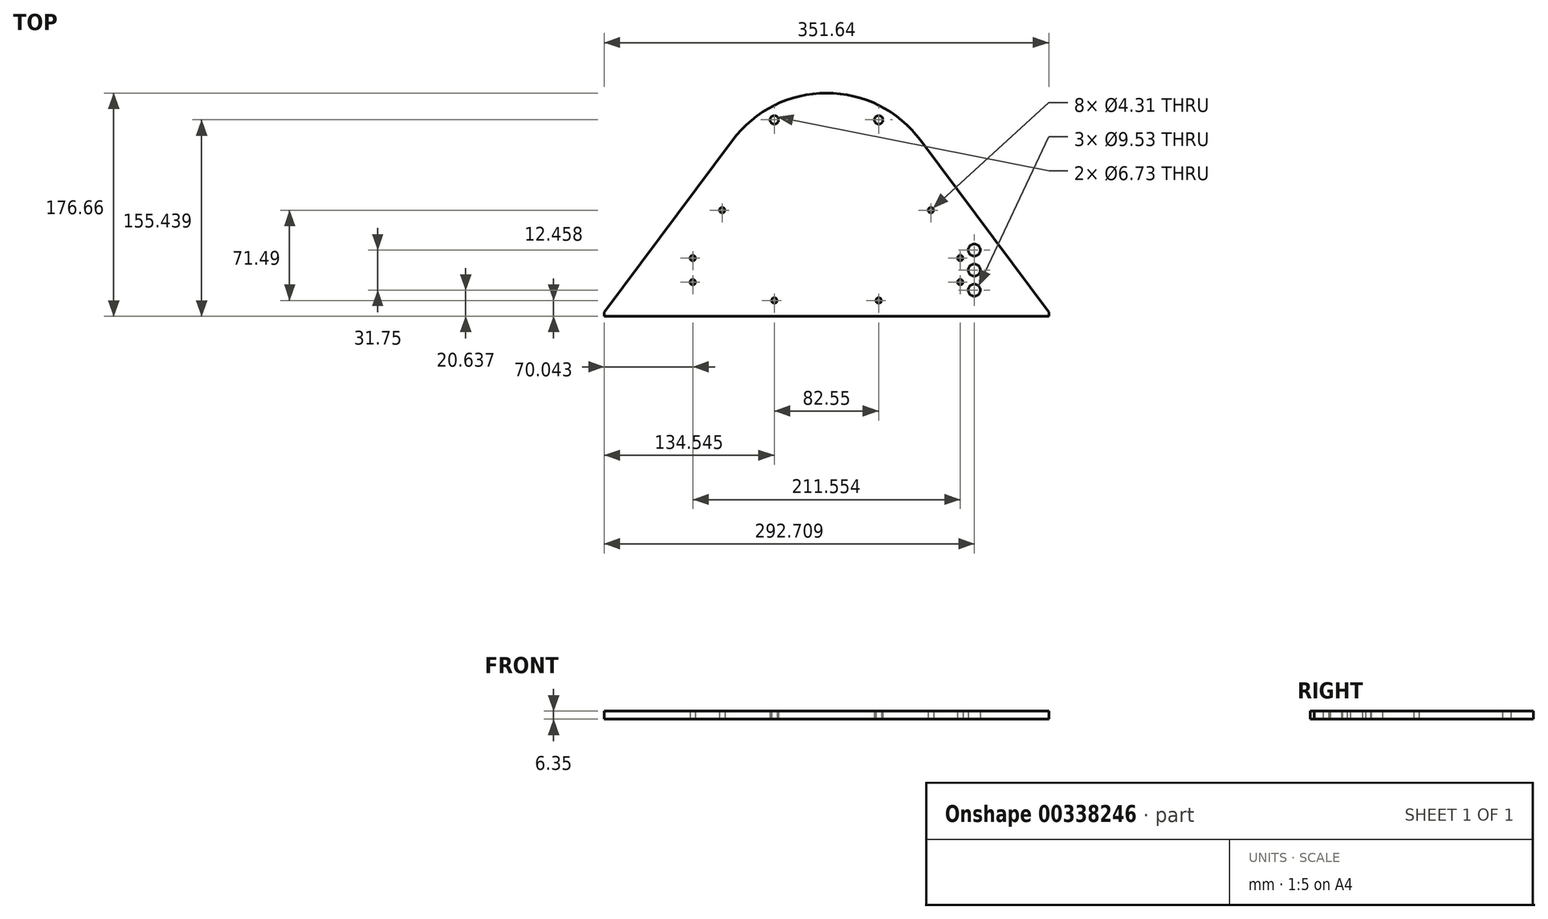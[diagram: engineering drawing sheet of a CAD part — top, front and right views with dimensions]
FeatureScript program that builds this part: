
annotation { "Feature Type Name" : "Feature", "Feature Type Description" : "" }
export const myFeature = defineFeature(function(context is Context, id is Id, definition is map)
    precondition{}
    {
        {
            var Q0;
            Q0=qCreatedBy(makeId("Top.planeOp"),FACE);
            var sketch = newSketch(context, id + "F0", { "sketchPlane" : qUnion([Q0])});
            skLineSegment(sketch, "E0", {"start": v(0, 0) * mm, "end": v(351.64, 0) * mm});
            skLineSegment(sketch, "E1", {"start": v(351.64, 0) * mm, "end": v(351.64, 3.18) * mm});
            skLineSegment(sketch, "E2", {"start": v(351.64, 3.17) * mm, "end": v(250.16, 139.35) * mm});
            skLineSegment(sketch, "E3", {"start": v(175.82, 0) * mm, "end": v(175.82, 83.95) * mm, "construction": true});
            skArc(sketch, "E4", {"start": v(250.16, 139.35) * mm, "mid": v(175.82, 176.66) * mm, "end": v(101.48, 139.35) * mm});
            skLineSegment(sketch, "E5", {"start": v(175.82, 83.95) * mm, "end": v(258.37, 83.95) * mm, "construction": true});
            skLineSegment(sketch, "E6", {"start": v(175.82, 83.95) * mm, "end": v(134.55, 155.44) * mm, "construction": true});
            skLineSegment(sketch, "E7", {"start": v(175.82, 83.95) * mm, "end": v(217.1, 155.44) * mm, "construction": true});
            skLineSegment(sketch, "E8", {"start": v(175.82, 83.95) * mm, "end": v(175.82, 155.44) * mm, "construction": true});
            skLineSegment(sketch, "E9", {"start": v(134.55, 155.44) * mm, "end": v(217.1, 155.44) * mm, "construction": true});
            skCircle(sketch, "E10", {"center": v(134.55, 155.44) * mm, "radius": 10.16 * mm, "construction": true});
            skLineSegment(sketch, "E11", {"start": v(0, 0) * mm, "end": v(0, 3.17) * mm});
            skLineSegment(sketch, "E12", {"start": v(0, 3.17) * mm, "end": v(101.48, 139.35) * mm});
            skLineSegment(sketch, "E13", {"start": v(175.82, 83.95) * mm, "end": v(217.1, 12.46) * mm, "construction": true});
            skLineSegment(sketch, "E14", {"start": v(217.1, 12.46) * mm, "end": v(258.37, 83.95) * mm, "construction": true});
            skLineSegment(sketch, "E15", {"start": v(258.37, 83.95) * mm, "end": v(217.1, 155.44) * mm, "construction": true});
            skLineSegment(sketch, "E16", {"start": v(134.55, 155.44) * mm, "end": v(93.27, 83.95) * mm, "construction": true});
            skLineSegment(sketch, "E17", {"start": v(93.27, 83.95) * mm, "end": v(175.82, 83.95) * mm, "construction": true});
            skLineSegment(sketch, "E18", {"start": v(175.82, 83.95) * mm, "end": v(134.55, 12.46) * mm, "construction": true});
            skLineSegment(sketch, "E19", {"start": v(134.55, 12.46) * mm, "end": v(93.27, 83.95) * mm, "construction": true});
            skCircle(sketch, "E20", {"center": v(134.55, 155.44) * mm, "radius": 3.37 * mm});
            skCircle(sketch, "E21", {"center": v(217.1, 155.44) * mm, "radius": 3.37 * mm});
            skCircle(sketch, "E22", {"center": v(93.27, 83.95) * mm, "radius": 2.15 * mm});
            skCircle(sketch, "E23", {"center": v(134.55, 12.46) * mm, "radius": 2.15 * mm});
            skCircle(sketch, "E24", {"center": v(217.1, 12.46) * mm, "radius": 2.15 * mm});
            skCircle(sketch, "E25", {"center": v(258.37, 83.95) * mm, "radius": 2.15 * mm});
            skLineSegment(sketch, "E26", {"start": v(281.6, 0) * mm, "end": v(281.6, 26.99) * mm, "construction": true});
            skLineSegment(sketch, "E27", {"start": v(281.6, 26.99) * mm, "end": v(281.6, 46.04) * mm, "construction": true});
            skCircle(sketch, "E28", {"center": v(281.6, 46.04) * mm, "radius": 2.15 * mm});
            skCircle(sketch, "E29", {"center": v(281.6, 26.99) * mm, "radius": 2.15 * mm});
            skLineSegment(sketch, "E30", {"start": v(70.04, 0) * mm, "end": v(70.04, 26.99) * mm, "construction": true});
            skLineSegment(sketch, "E31", {"start": v(70.04, 26.99) * mm, "end": v(70.04, 46.04) * mm, "construction": true});
            skLineSegment(sketch, "E32", {"start": v(70.04, 46.04) * mm, "end": v(31.94, 46.04) * mm, "construction": true});
            skCircle(sketch, "E33", {"center": v(70.04, 46.04) * mm, "radius": 2.15 * mm});
            skCircle(sketch, "E34", {"center": v(70.04, 26.99) * mm, "radius": 2.15 * mm});
            skLineSegment(sketch, "E35", {"start": v(281.6, 46.04) * mm, "end": v(319.7, 46.04) * mm, "construction": true});
            skLineSegment(sketch, "E36", {"start": v(281.6, 36.51) * mm, "end": v(292.7, 36.51) * mm, "construction": true});
            skLineSegment(sketch, "E37", {"start": v(292.7, 52.39) * mm, "end": v(292.7, 20.64) * mm, "construction": true});
            skCircle(sketch, "E38", {"center": v(292.7, 52.39) * mm, "radius": 4.76 * mm});
            skCircle(sketch, "E39", {"center": v(292.7, 36.51) * mm, "radius": 4.76 * mm});
            skCircle(sketch, "E40", {"center": v(292.7, 20.64) * mm, "radius": 4.76 * mm});
            skSolve(sketch);
        }
        {
            var Q0;
            Q0=qSketchRegion(id+"F0",true);
            extrude(context, id + "F1", {"entities" : qUnion([Q0]), "depth" : 6.35 * mm});
        }
    });
